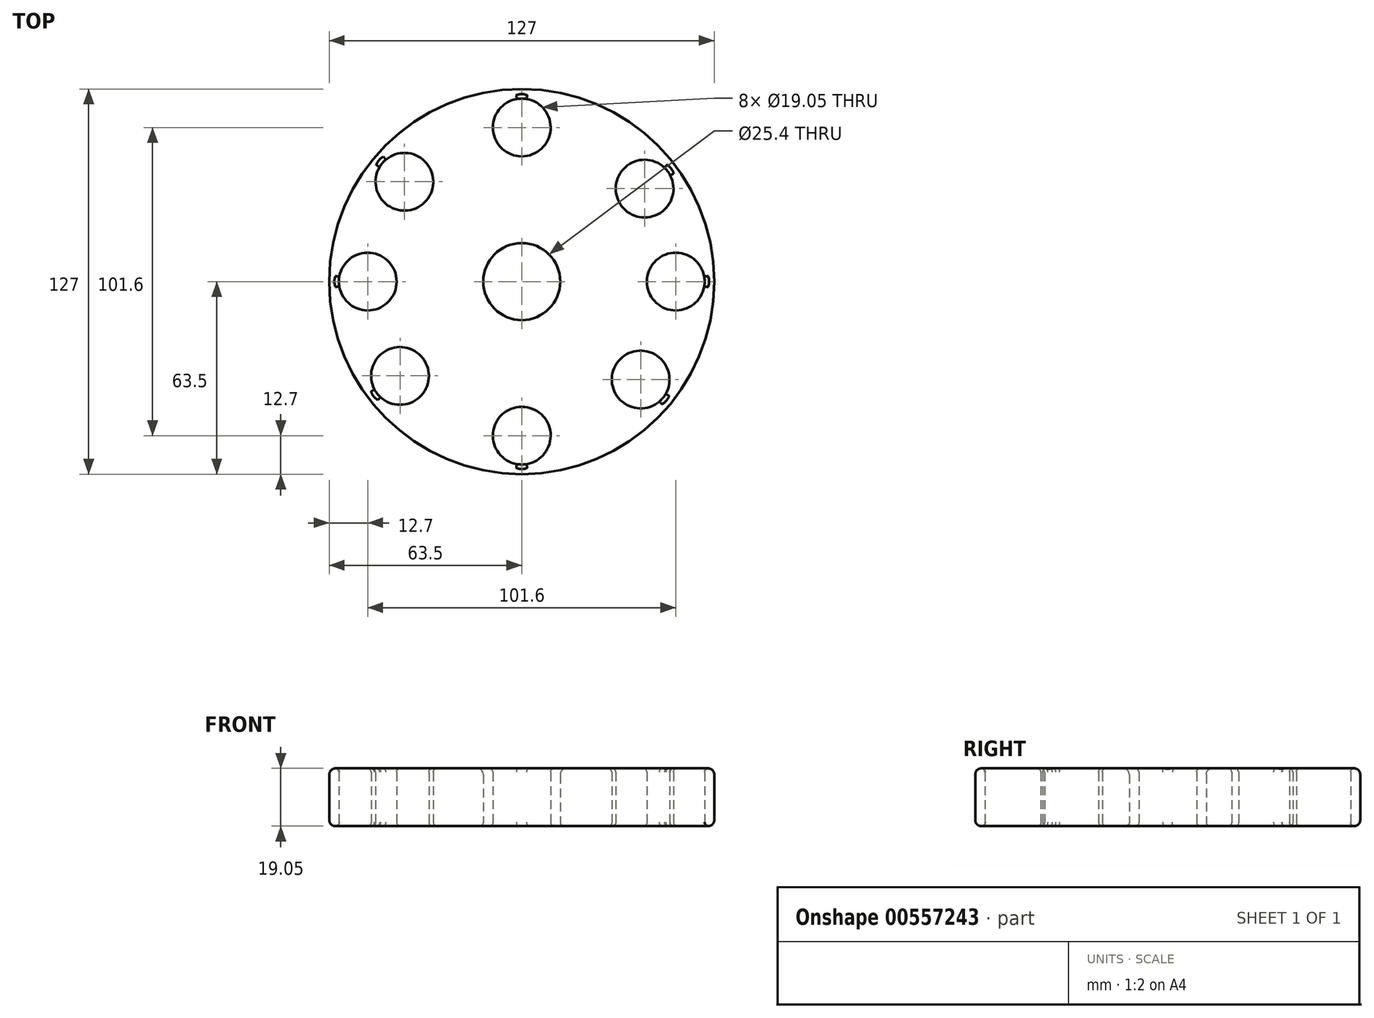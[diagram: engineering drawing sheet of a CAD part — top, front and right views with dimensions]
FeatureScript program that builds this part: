
annotation { "Feature Type Name" : "Feature", "Feature Type Description" : "" }
export const myFeature = defineFeature(function(context is Context, id is Id, definition is map)
    precondition{}
    {
        {
            var Q0;
            Q0=qCreatedBy(makeId("Top.planeOp"),FACE);
            var sketch = newSketch(context, id + "F0", { "sketchPlane" : qUnion([Q0])});
            skCircle(sketch, "E0", {"center": v(0, 0) * mm, "radius": 63.5 * mm});
            skLineSegment(sketch, "E1", {"start": v(0, 63.5) * mm, "end": v(0, -63.5) * mm});
            skLineSegment(sketch, "E2", {"start": v(-50.25, -38.82) * mm, "end": v(50.61, 38.35) * mm});
            skLineSegment(sketch, "E3", {"start": v(-48.44, 41.06) * mm, "end": v(48.95, -40.44) * mm});
            skCircle(sketch, "E4", {"center": v(-38.7, 32.9) * mm, "radius": 9.53 * mm});
            skCircle(sketch, "E5", {"center": v(0, 50.8) * mm, "radius": 9.53 * mm});
            skCircle(sketch, "E6", {"center": v(40.52, 30.63) * mm, "radius": 9.53 * mm});
            skCircle(sketch, "E7", {"center": v(39.21, -32.3) * mm, "radius": 9.53 * mm});
            skCircle(sketch, "E8", {"center": v(0, -50.8) * mm, "radius": 9.53 * mm});
            skCircle(sketch, "E9", {"center": v(-40.17, -31.1) * mm, "radius": 9.53 * mm});
            skLineSegment(sketch, "E10", {"start": v(-63.5, 0) * mm, "end": v(63.5, 0) * mm});
            skCircle(sketch, "E11", {"center": v(-50.8, 0) * mm, "radius": 9.53 * mm});
            skCircle(sketch, "E12", {"center": v(50.8, 0) * mm, "radius": 9.53 * mm});
            skCircle(sketch, "E13", {"center": v(0, 0) * mm, "radius": 12.7 * mm});
            skSolve(sketch);
        }
        {
            var Q0;
            {var subQ1=sQuery(id+"F0.wireOp",EDGE,"E1");var subQ6=sQuery(id+"F0.wireOp",EDGE,"E0");var subQ11=makeQuery(id+"F0.imprint","INTERSECT",VERTEX,{"disambiguationData":[OD(0.0)],"derivedFrom":[subQ6,subQ1]});Q0=makeQuery(id+"F0.imprint","IMPRINT",FACE,{"disambiguationData":[TD([[makeQuery(id+"F0.imprint","IMPRINT",EDGE,{"disambiguationData":[TD([[subQ11,-1.0]])],"derivedFrom":subQ6}),1.0]])]});}
            var Q1;
            {var subQ1=sQuery(id+"F0.wireOp",EDGE,"E3");var subQ11=sQuery(id+"F0.wireOp",EDGE,"E0");var subQ12=makeQuery(id+"F0.imprint","INTERSECT",VERTEX,{"disambiguationData":[OD(0.0)],"derivedFrom":[subQ11,subQ1]});Q1=makeQuery(id+"F0.imprint","IMPRINT",FACE,{"disambiguationData":[TD([[makeQuery(id+"F0.imprint","IMPRINT",EDGE,{"disambiguationData":[TD([[subQ12,-1.0]])],"derivedFrom":subQ11}),1.0]])]});}
            var Q2;
            {var subQ1=sQuery(id+"F0.wireOp",EDGE,"E2");var subQ6=sQuery(id+"F0.wireOp",EDGE,"E0");var subQ7=makeQuery(id+"F0.imprint","INTERSECT",VERTEX,{"disambiguationData":[OD(0.0)],"derivedFrom":[subQ6,subQ1]});Q2=makeQuery(id+"F0.imprint","IMPRINT",FACE,{"disambiguationData":[TD([[makeQuery(id+"F0.imprint","IMPRINT",EDGE,{"disambiguationData":[TD([[subQ7,1.0]])],"derivedFrom":subQ6}),1.0]])]});}
            var Q3;
            {var subQ1=sQuery(id+"F0.wireOp",EDGE,"E0");var subQ5=sQuery(id+"F0.wireOp",EDGE,"E1");var subQ6=makeQuery(id+"F0.imprint","INTERSECT",VERTEX,{"disambiguationData":[OD(1.0)],"derivedFrom":[subQ1,subQ5]});Q3=makeQuery(id+"F0.imprint","IMPRINT",FACE,{"disambiguationData":[TD([[makeQuery(id+"F0.imprint","IMPRINT",EDGE,{"disambiguationData":[TD([[subQ6,1.0]])],"derivedFrom":subQ1}),1.0]])]});}
            var Q4;
            {var subQ0=sQuery(id+"F0.wireOp",EDGE,"E1");var subQ1=sQuery(id+"F0.wireOp",EDGE,"E0");var subQ2=makeQuery(id+"F0.imprint","INTERSECT",VERTEX,{"disambiguationData":[OD(1.0)],"derivedFrom":[subQ1,subQ0]});Q4=makeQuery(id+"F0.imprint","IMPRINT",FACE,{"disambiguationData":[TD([[makeQuery(id+"F0.imprint","IMPRINT",EDGE,{"disambiguationData":[TD([[subQ2,-1.0]])],"derivedFrom":subQ1}),1.0]])]});}
            var Q5;
            {var subQ1=sQuery(id+"F0.wireOp",EDGE,"E3");var subQ10=sQuery(id+"F0.wireOp",EDGE,"E0");var subQ11=makeQuery(id+"F0.imprint","INTERSECT",VERTEX,{"disambiguationData":[OD(1.0)],"derivedFrom":[subQ10,subQ1]});Q5=makeQuery(id+"F0.imprint","IMPRINT",FACE,{"disambiguationData":[TD([[makeQuery(id+"F0.imprint","IMPRINT",EDGE,{"disambiguationData":[TD([[subQ11,-1.0]])],"derivedFrom":subQ10}),1.0]])]});}
            var Q6;
            {var subQ1=sQuery(id+"F0.wireOp",EDGE,"E2");var subQ4=sQuery(id+"F0.wireOp",EDGE,"E0");var subQ5=makeQuery(id+"F0.imprint","INTERSECT",VERTEX,{"disambiguationData":[OD(1.0)],"derivedFrom":[subQ4,subQ1]});Q6=makeQuery(id+"F0.imprint","IMPRINT",FACE,{"disambiguationData":[TD([[makeQuery(id+"F0.imprint","IMPRINT",EDGE,{"disambiguationData":[TD([[subQ5,1.0]])],"derivedFrom":subQ4}),1.0]])]});}
            var Q7;
            {var subQ6=sQuery(id+"F0.wireOp",EDGE,"E1");var subQ9=sQuery(id+"F0.wireOp",EDGE,"E0");var subQ10=makeQuery(id+"F0.imprint","INTERSECT",VERTEX,{"disambiguationData":[OD(0.0)],"derivedFrom":[subQ9,subQ6]});Q7=makeQuery(id+"F0.imprint","IMPRINT",FACE,{"disambiguationData":[TD([[makeQuery(id+"F0.imprint","IMPRINT",EDGE,{"disambiguationData":[TD([[subQ10,1.0]])],"derivedFrom":subQ9}),1.0]])]});}
            extrude(context, id + "F1", {"entities" : qUnion([Q0, Q1, Q2, Q3, Q4, Q5, Q6, Q7]), "depth" : 19.05 * mm, "offsetDistance" : 25.4 * mm});
        }
        {
            var Q0;
            Q0=makeQuery(id+"F1.opExtrude","CAP_EDGE",EDGE,{"disambiguationData":[OSD([sQuery(id+"F0.wireOp",EDGE,"E0")])],"isStart":false});
            fillet(context, id + "F2", {"entities" : qUnion([Q0]), "radius" : 2.03 * mm, "tangentPropagation" : true, "allowEdgeOverflow" : false});
        }
        {
            var Q0;
            Q0=makeQuery(id+"F1.opExtrude","CAP_EDGE",EDGE,{"disambiguationData":[OSD([sQuery(id+"F0.wireOp",EDGE,"E0")])],"isStart":true});
            var Q1;
            Q1=makeQuery(id+"F1.opExtrude","CAP_EDGE",EDGE,{"disambiguationData":[OSD([sQuery(id+"F0.wireOp",EDGE,"E13")])],"isStart":false});
            fillet(context, id + "F3", {"entities" : qUnion([Q0, Q1]), "radius" : 2.03 * mm, "tangentPropagation" : true, "allowEdgeOverflow" : false});
        }
        {
            var Q0;
            Q0=makeQuery(id+"F1.opExtrude","CAP_EDGE",EDGE,{"disambiguationData":[OSD([sQuery(id+"F0.wireOp",EDGE,"E9")])],"isStart":false});
            var Q1;
            Q1=makeQuery(id+"F1.opExtrude","CAP_EDGE",EDGE,{"disambiguationData":[OSD([sQuery(id+"F0.wireOp",EDGE,"E11")])],"isStart":false});
            var Q2;
            Q2=makeQuery(id+"F1.opExtrude","CAP_EDGE",EDGE,{"disambiguationData":[OSD([sQuery(id+"F0.wireOp",EDGE,"E4")])],"isStart":false});
            var Q3;
            Q3=makeQuery(id+"F1.opExtrude","CAP_EDGE",EDGE,{"disambiguationData":[OSD([sQuery(id+"F0.wireOp",EDGE,"E5")])],"isStart":false});
            var Q4;
            Q4=makeQuery(id+"F1.opExtrude","CAP_EDGE",EDGE,{"disambiguationData":[OSD([sQuery(id+"F0.wireOp",EDGE,"E6")])],"isStart":false});
            var Q5;
            Q5=makeQuery(id+"F1.opExtrude","CAP_EDGE",EDGE,{"disambiguationData":[OSD([sQuery(id+"F0.wireOp",EDGE,"E12")])],"isStart":false});
            var Q6;
            Q6=makeQuery(id+"F1.opExtrude","CAP_EDGE",EDGE,{"disambiguationData":[OSD([sQuery(id+"F0.wireOp",EDGE,"E7")])],"isStart":false});
            var Q7;
            Q7=makeQuery(id+"F1.opExtrude","CAP_EDGE",EDGE,{"disambiguationData":[OSD([sQuery(id+"F0.wireOp",EDGE,"E8")])],"isStart":false});
            fillet(context, id + "F4", {"entities" : qUnion([Q0, Q1, Q2, Q3, Q4, Q5, Q6, Q7]), "radius" : 1.27 * mm, "tangentPropagation" : true, "allowEdgeOverflow" : false});
        }
        {
            var Q0;
            Q0=makeQuery(id+"F1.opExtrude","CAP_EDGE",EDGE,{"disambiguationData":[OSD([sQuery(id+"F0.wireOp",EDGE,"E6")])],"isStart":true});
            var Q1;
            Q1=makeQuery(id+"F1.opExtrude","CAP_EDGE",EDGE,{"disambiguationData":[OSD([sQuery(id+"F0.wireOp",EDGE,"E5")])],"isStart":true});
            var Q2;
            Q2=makeQuery(id+"F1.opExtrude","CAP_EDGE",EDGE,{"disambiguationData":[OSD([sQuery(id+"F0.wireOp",EDGE,"E13")])],"isStart":true});
            var Q3;
            Q3=makeQuery(id+"F1.opExtrude","CAP_EDGE",EDGE,{"disambiguationData":[OSD([sQuery(id+"F0.wireOp",EDGE,"E7")])],"isStart":true});
            var Q4;
            Q4=makeQuery(id+"F1.opExtrude","CAP_EDGE",EDGE,{"disambiguationData":[OSD([sQuery(id+"F0.wireOp",EDGE,"E12")])],"isStart":true});
            var Q5;
            Q5=makeQuery(id+"F1.opExtrude","CAP_EDGE",EDGE,{"disambiguationData":[OSD([sQuery(id+"F0.wireOp",EDGE,"E8")])],"isStart":true});
            var Q6;
            Q6=makeQuery(id+"F1.opExtrude","CAP_EDGE",EDGE,{"disambiguationData":[OSD([sQuery(id+"F0.wireOp",EDGE,"E9")])],"isStart":true});
            var Q7;
            Q7=makeQuery(id+"F1.opExtrude","CAP_EDGE",EDGE,{"disambiguationData":[OSD([sQuery(id+"F0.wireOp",EDGE,"E11")])],"isStart":true});
            var Q8;
            Q8=makeQuery(id+"F1.opExtrude","CAP_EDGE",EDGE,{"disambiguationData":[OSD([sQuery(id+"F0.wireOp",EDGE,"E4")])],"isStart":true});
            fillet(context, id + "F5", {"entities" : qUnion([Q0, Q1, Q2, Q3, Q4, Q5, Q6, Q7, Q8]), "radius" : 1.27 * mm, "tangentPropagation" : true, "allowEdgeOverflow" : false});
        }
    });
